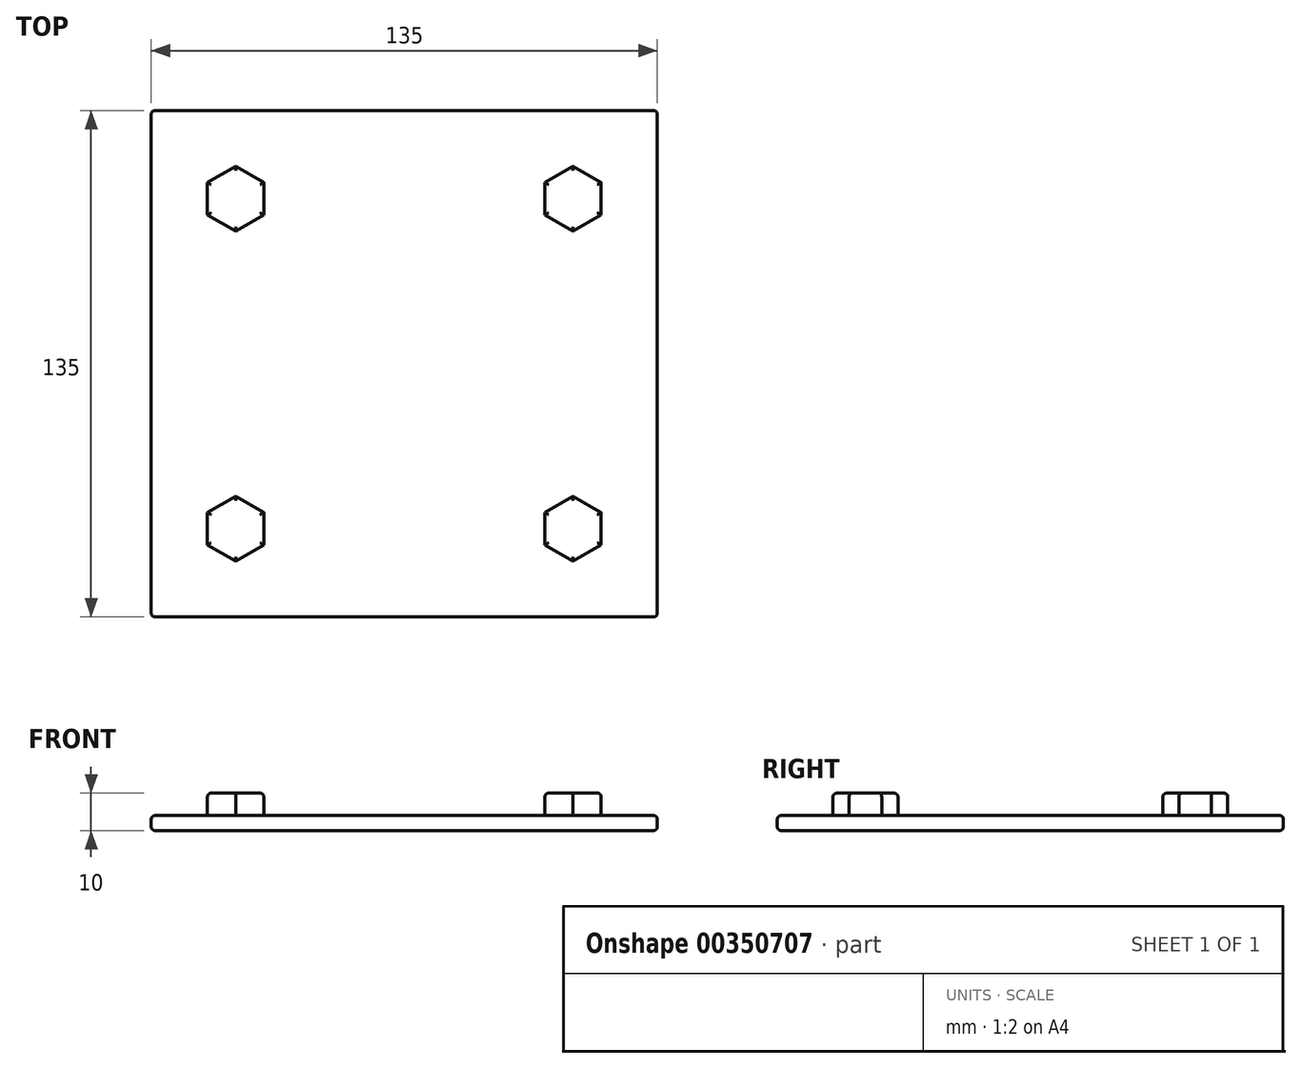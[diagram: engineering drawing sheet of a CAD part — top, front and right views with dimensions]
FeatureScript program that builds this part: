
annotation { "Feature Type Name" : "Feature", "Feature Type Description" : "" }
export const myFeature = defineFeature(function(context is Context, id is Id, definition is map)
    precondition{}
    {
        {
            var Q0;
            Q0=qCreatedBy(makeId("Top.planeOp"),FACE);
            var sketch = newSketch(context, id + "F0", { "sketchPlane" : qUnion([Q0])});
            skLineSegment(sketch, "E0", {"start": v(0, 0) * mm, "end": v(0, 135) * mm});
            skLineSegment(sketch, "E1", {"start": v(0, 135) * mm, "end": v(135, 135) * mm});
            skLineSegment(sketch, "E2", {"start": v(135, 135) * mm, "end": v(135, 0) * mm});
            skLineSegment(sketch, "E3", {"start": v(135, 0) * mm, "end": v(0, 0) * mm});
            skSolve(sketch);
        }
        {
            var Q0;
            Q0 = qSketchRegion(id + "F0", true);
            extrude(context, id + "F1", {"entities" : qUnion([Q0]), "depth" : 4 * mm});
        }
        {
            var Q0;
            Q0=makeQuery(id+"F1.opExtrude","CAP_FACE",FACE,{"disambiguationData":[OSD([sQuery(id+"F0.wireOp",EDGE,"E0"),sQuery(id+"F0.wireOp",EDGE,"E1"),sQuery(id+"F0.wireOp",EDGE,"E2"),sQuery(id+"F0.wireOp",EDGE,"E3")])],"isStart":false});
            var Q1;
            Q1=makeQuery(id+"F1.opExtrude","CAP_FACE",FACE,{"disambiguationData":[OSD([sQuery(id+"F0.wireOp",EDGE,"E0"),sQuery(id+"F0.wireOp",EDGE,"E1"),sQuery(id+"F0.wireOp",EDGE,"E2"),sQuery(id+"F0.wireOp",EDGE,"E3")])],"isStart":true});
            var Q2;
            Q2=makeQuery(id+"F1.opExtrude","SWEPT_EDGE",EDGE,{"disambiguationData":[OSD([sQuery(id+"F0.wireOp",EDGE,"E2"),sQuery(id+"F0.wireOp",EDGE,"E3")])]});
            var Q3;
            Q3=makeQuery(id+"F1.opExtrude","SWEPT_EDGE",EDGE,{"disambiguationData":[OSD([sQuery(id+"F0.wireOp",EDGE,"E0"),sQuery(id+"F0.wireOp",EDGE,"E3")])]});
            var Q4;
            Q4=makeQuery(id+"F1.opExtrude","SWEPT_EDGE",EDGE,{"disambiguationData":[OSD([sQuery(id+"F0.wireOp",EDGE,"E1"),sQuery(id+"F0.wireOp",EDGE,"E2")])]});
            var Q5;
            Q5=makeQuery(id+"F1.opExtrude","SWEPT_EDGE",EDGE,{"disambiguationData":[OSD([sQuery(id+"F0.wireOp",EDGE,"E0"),sQuery(id+"F0.wireOp",EDGE,"E1")])]});
            fillet(context, id + "F2", {"entities" : qUnion([Q0, Q1, Q2, Q3, Q4, Q5]), "radius" : 1 * mm, "tangentPropagation" : true, "allowEdgeOverflow" : false});
        }
        {
            var Q0;
            Q0=makeQuery(id+"F1.opExtrude","CAP_FACE",FACE,{"disambiguationData":[OSD([sQuery(id+"F0.wireOp",EDGE,"E0"),sQuery(id+"F0.wireOp",EDGE,"E1"),sQuery(id+"F0.wireOp",EDGE,"E2"),sQuery(id+"F0.wireOp",EDGE,"E3")])],"isStart":false});
            var sketch = newSketch(context, id + "F3", { "sketchPlane" : qUnion([Q0])});
            skCircle(sketch, "E4.cCircle", {"center": v(22.5, 111.5) * mm, "radius": 7.5 * mm, "construction": true});
            skLineSegment(sketch, "E4.0", {"start": v(30, 107.17) * mm, "end": v(22.5, 102.84) * mm});
            skLineSegment(sketch, "E4.1", {"start": v(22.5, 102.84) * mm, "end": v(15, 107.17) * mm});
            skLineSegment(sketch, "E4.2", {"start": v(15, 107.17) * mm, "end": v(15, 115.83) * mm});
            skLineSegment(sketch, "E4.3", {"start": v(15, 115.83) * mm, "end": v(22.5, 120.16) * mm});
            skLineSegment(sketch, "E4.4", {"start": v(22.5, 120.16) * mm, "end": v(30, 115.83) * mm});
            skLineSegment(sketch, "E4.5", {"start": v(30, 115.83) * mm, "end": v(30, 107.17) * mm});
            skPoint(sketch, "E4.0.midPoint", {"position": v(26.25, 105) * mm});
            skLineSegment(sketch, "E5", {"start": v(67.5, 134) * mm, "end": v(67.5, 1) * mm, "construction": true});
            skLineSegment(sketch, "E6", {"start": v(1, 67.5) * mm, "end": v(134, 67.5) * mm, "construction": true});
            skLineSegment(sketch, "E7.MirrorCS", {"start": v(112.5, 120.16) * mm, "end": v(105, 115.83) * mm});
            skLineSegment(sketch, "E8.MirrorCS", {"start": v(120, 115.83) * mm, "end": v(112.5, 120.16) * mm});
            skLineSegment(sketch, "E9.MirrorCS", {"start": v(120, 107.17) * mm, "end": v(120, 115.83) * mm});
            skLineSegment(sketch, "E10.MirrorCS", {"start": v(112.5, 102.84) * mm, "end": v(120, 107.17) * mm});
            skLineSegment(sketch, "E11.MirrorCS", {"start": v(105, 115.83) * mm, "end": v(105, 107.17) * mm});
            skLineSegment(sketch, "E12.MirrorCS", {"start": v(105, 107.17) * mm, "end": v(112.5, 102.84) * mm});
            skPoint(sketch, "E13.MirrorP", {"position": v(108.75, 105) * mm});
            skCircle(sketch, "E14.MirrorC", {"center": v(112.5, 111.5) * mm, "radius": 7.5 * mm, "construction": true});
            skLineSegment(sketch, "E15.MirrorCS", {"start": v(134, 67.5) * mm, "end": v(1, 67.5) * mm, "construction": true});
            skLineSegment(sketch, "E16.MirrorCS", {"start": v(30, 27.83) * mm, "end": v(22.5, 32.16) * mm});
            skLineSegment(sketch, "E17.MirrorCS", {"start": v(15, 19.17) * mm, "end": v(22.5, 14.84) * mm});
            skLineSegment(sketch, "E18.MirrorCS", {"start": v(22.5, 32.16) * mm, "end": v(15, 27.83) * mm});
            skLineSegment(sketch, "E19.MirrorCS", {"start": v(15, 27.83) * mm, "end": v(15, 19.17) * mm});
            skLineSegment(sketch, "E20.MirrorCS", {"start": v(22.5, 14.84) * mm, "end": v(30, 19.17) * mm});
            skPoint(sketch, "E21.MirrorP", {"position": v(26.25, 30) * mm});
            skCircle(sketch, "E22.MirrorC", {"center": v(22.5, 23.5) * mm, "radius": 7.5 * mm, "construction": true});
            skLineSegment(sketch, "E23.MirrorCS", {"start": v(30, 19.17) * mm, "end": v(30, 27.83) * mm});
            skLineSegment(sketch, "E24.MirrorCS", {"start": v(112.5, 14.84) * mm, "end": v(105, 19.17) * mm});
            skLineSegment(sketch, "E25.MirrorCS", {"start": v(105, 27.83) * mm, "end": v(112.5, 32.16) * mm});
            skLineSegment(sketch, "E26.MirrorCS", {"start": v(120, 27.83) * mm, "end": v(120, 19.17) * mm});
            skLineSegment(sketch, "E27.MirrorCS", {"start": v(112.5, 32.16) * mm, "end": v(120, 27.83) * mm});
            skLineSegment(sketch, "E28.MirrorCS", {"start": v(120, 19.17) * mm, "end": v(112.5, 14.84) * mm});
            skPoint(sketch, "E29.MirrorP", {"position": v(108.75, 30) * mm});
            skLineSegment(sketch, "E30.MirrorCS", {"start": v(105, 19.17) * mm, "end": v(105, 27.83) * mm});
            skCircle(sketch, "E31.MirrorC", {"center": v(112.5, 23.5) * mm, "radius": 7.5 * mm, "construction": true});
            skSolve(sketch);
        }
        {
            var Q0;
            Q0 = qSketchRegion(id + "F3", true);
            extrude(context, id + "F4", {"entities" : qUnion([Q0]), "operationType" : NewBodyOperationType.ADD, "depth" : 6 * mm});
        }
        {
            var Q0;
            Q0=makeQuery(id+"F4.opExtrude","CAP_FACE",FACE,{"disambiguationData":[OSD([sQuery(id+"F3.wireOp",EDGE,"E4.1"),sQuery(id+"F3.wireOp",EDGE,"E4.0"),sQuery(id+"F3.wireOp",EDGE,"E4.5"),sQuery(id+"F3.wireOp",EDGE,"E4.2"),sQuery(id+"F3.wireOp",EDGE,"E4.4"),sQuery(id+"F3.wireOp",EDGE,"E4.3")])],"isStart":false});
            var Q1;
            Q1=makeQuery(id+"F4.opExtrude","CAP_FACE",FACE,{"disambiguationData":[OSD([sQuery(id+"F3.wireOp",EDGE,"E12.MirrorCS"),sQuery(id+"F3.wireOp",EDGE,"E10.MirrorCS"),sQuery(id+"F3.wireOp",EDGE,"E11.MirrorCS"),sQuery(id+"F3.wireOp",EDGE,"E7.MirrorCS"),sQuery(id+"F3.wireOp",EDGE,"E9.MirrorCS"),sQuery(id+"F3.wireOp",EDGE,"E8.MirrorCS")])],"isStart":false});
            var Q2;
            Q2=makeQuery(id+"F4.opExtrude","CAP_FACE",FACE,{"disambiguationData":[OSD([sQuery(id+"F3.wireOp",EDGE,"E27.MirrorCS"),sQuery(id+"F3.wireOp",EDGE,"E26.MirrorCS"),sQuery(id+"F3.wireOp",EDGE,"E24.MirrorCS"),sQuery(id+"F3.wireOp",EDGE,"E28.MirrorCS"),sQuery(id+"F3.wireOp",EDGE,"E25.MirrorCS"),sQuery(id+"F3.wireOp",EDGE,"E30.MirrorCS")])],"isStart":false});
            var Q3;
            Q3=makeQuery(id+"F4.opExtrude","CAP_FACE",FACE,{"disambiguationData":[OSD([sQuery(id+"F3.wireOp",EDGE,"E16.MirrorCS"),sQuery(id+"F3.wireOp",EDGE,"E17.MirrorCS"),sQuery(id+"F3.wireOp",EDGE,"E18.MirrorCS"),sQuery(id+"F3.wireOp",EDGE,"E23.MirrorCS"),sQuery(id+"F3.wireOp",EDGE,"E20.MirrorCS"),sQuery(id+"F3.wireOp",EDGE,"E19.MirrorCS")])],"isStart":false});
            fillet(context, id + "F5", {"entities" : qUnion([Q0, Q1, Q2, Q3]), "radius" : 1 * mm, "tangentPropagation" : true, "allowEdgeOverflow" : false});
        }
    });
